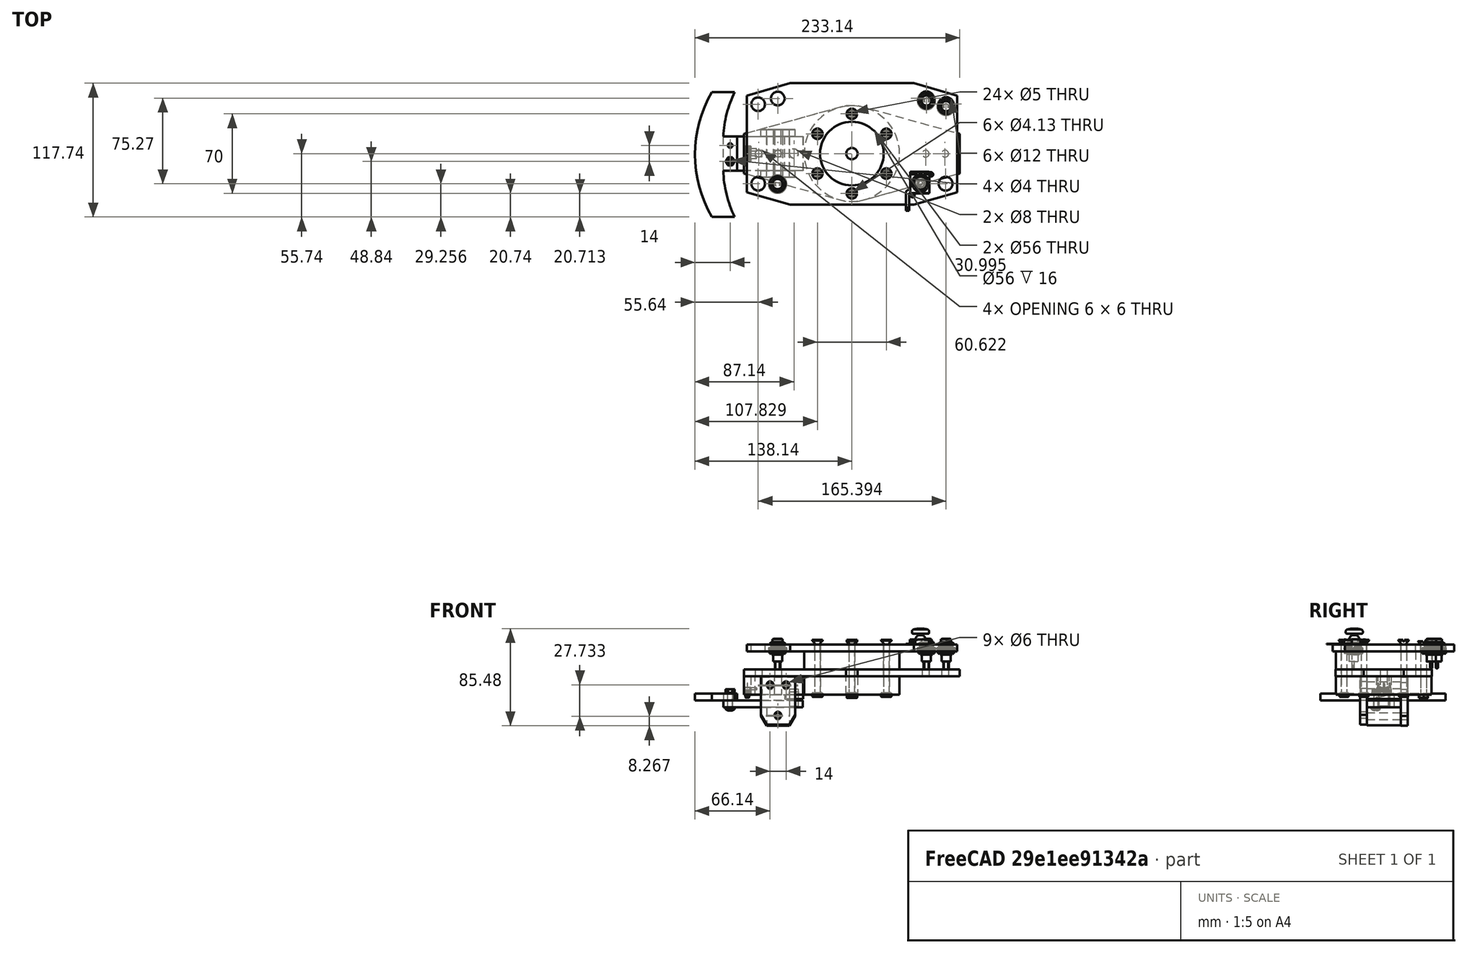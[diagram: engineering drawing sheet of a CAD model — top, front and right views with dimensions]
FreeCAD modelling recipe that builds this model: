
FCSTD DOCUMENT  (FreeCAD 0.19R24267 +99 (Git))
Label: Wheel
License: All rights reserved
LicenseURL: http://en.wikipedia.org/wiki/All_rights_reserved
objects: TechDraw::DrawViewDimension×38, Part::FeaturePython×16, TechDraw::DrawProjGroupItem×10, Sketcher::SketchObject×6, PartDesign::Pocket×6, App::Part×5, TechDraw::DrawProjGroup×5, PartDesign::Pad×4, PartDesign::ShapeBinder×4, PartDesign::Body×4, Part::Feature×3, TechDraw::DrawSVGTemplate×3, TechDraw::DrawPage×3, App::Link×2, PartDesign::SubShapeBinder×2, App::DocumentObjectGroup×1, Part::Mirroring×1
note: 56 computed .brp shape members not serialized (recipe doc carries the construction recipe); baked Part::Feature solids carry a one-line shape summary decoded from their .brp
EXTERNAL_REF file=PaddleShifter.FCStd obj=Part
EXTERNAL_REF file=PaddleShifter-v2.FCStd obj=Part

FEATURE [Part::Feature] steering_wheel_momo_team  label="steering_wheel_momo_team 300mm"
  Placement = pos=(3.67046e-10,8.97259,34) rot=(0,0,1;0rad)
  shape: bbox 319 x 576 x 33.23 mm, 603 faces, 0 solids (baked)
FEATURE [Sketcher::SketchObject] Sketch
  FullyConstrained = true
  MapMode = 5
  Support = -> [XY_Plane001]
  sketch-geometry (17):
    g0: Circle CenterX=-30.3109 CenterY=17.5 CenterZ=0 NormalX=0 NormalY=0 NormalZ=1 AngleXU=0 Radius=2.5
    g1: Circle CenterX=0 CenterY=35 CenterZ=0 NormalX=0 NormalY=0 NormalZ=1 AngleXU=0 Radius=2.5
    g2: Circle CenterX=30.3109 CenterY=17.5 CenterZ=0 NormalX=0 NormalY=0 NormalZ=1 AngleXU=0 Radius=2.5
    g3: Circle CenterX=30.3109 CenterY=-17.5 CenterZ=0 NormalX=0 NormalY=0 NormalZ=1 AngleXU=0 Radius=2.5
    g4: Circle CenterX=0 CenterY=-35 CenterZ=0 NormalX=0 NormalY=0 NormalZ=1 AngleXU=0 Radius=2.5
    g5: Circle CenterX=-30.3109 CenterY=-17.5 CenterZ=0 NormalX=0 NormalY=0 NormalZ=1 AngleXU=0 Radius=2.5
    g6: Circle CenterX=0 CenterY=0 CenterZ=0 NormalX=0 NormalY=0 NormalZ=1 AngleXU=0 Radius=35
    g7: LineSegment StartX=-30.3109 StartY=-17.5 StartZ=0 EndX=-30.3109 EndY=17.5 EndZ=0
    g8: LineSegment StartX=-30.3109 StartY=17.5 StartZ=0 EndX=0 EndY=35 EndZ=0
    g9: LineSegment StartX=0 StartY=35 StartZ=0 EndX=30.3109 EndY=17.5 EndZ=0
    g10: LineSegment StartX=30.3109 StartY=17.5 StartZ=0 EndX=30.3109 EndY=-17.5 EndZ=0
    g11: LineSegment StartX=30.3109 StartY=-17.5 StartZ=0 EndX=0 EndY=-35 EndZ=0
    g12: LineSegment StartX=-30.3109 StartY=-17.5 StartZ=0 EndX=0 EndY=-35 EndZ=0
    g13: Circle CenterX=0 CenterY=0 CenterZ=0 NormalX=0 NormalY=0 NormalZ=1 AngleXU=0 Radius=28
    g14: Circle CenterX=0 CenterY=0 CenterZ=0 NormalX=0 NormalY=0 NormalZ=1 AngleXU=0 Radius=42
    g15: LineSegment StartX=0 StartY=35 StartZ=0 EndX=0 EndY=42 EndZ=0
    g16: LineSegment StartX=0 StartY=35 StartZ=0 EndX=0 EndY=28 EndZ=0
  constraints (42):
    c: PointOnObject(g2,g6)
    c: PointOnObject(g1,g6)
    c: Coincident(g7,g5)
    c: Coincident(g7,g0)
    c: Coincident(g8,g0)
    c: Coincident(g8,g1)
    c: Coincident(g9,g1)
    c: Coincident(g9,g2)
    c: Coincident(g10,g2)
    c: Coincident(g10,g3)
    c: Coincident(g11,g3)
    c: Coincident(g11,g4)
    c: Coincident(g12,g5)
    c: Coincident(g12,g4)
    c: Coincident(g13,g6)
    c: Coincident(g14,g13)
    c: Coincident(g15,g1)
    c: PointOnObject(g15,g14)
    c: Vertical(g15)
    c: Coincident(g16,g1)
    c: PointOnObject(g16,g13)
    c: Vertical(g16)
    c: Equal(g15,g16)
    c: DistanceY(g15,g15) = 7
    c: Equal(g9,g8)
    c: Equal(g8,g7)
    c: Equal(g7,g12)
    c: Equal(g12,g11)
    c: Equal(g11,g10)
    c: Diameter(g1) = 5
    c: Equal(g1,g0)
    c: Equal(g0,g5)
    c: Equal(g5,g4)
    c: Equal(g4,g3)
    c: Equal(g3,g2)
    c: PointOnObject(g3,g6)
    c: PointOnObject(g4,g6)
    c: PointOnObject(g5,g6)
    c: PointOnObject(g1,g-2)
    c: PointOnObject(g4,g-2)
    c: Coincident(g-1,g13)
    c: Diameter(g6) = 70
FEATURE [PartDesign::Pad] Pad
  Direction = (1,1,1)
  Length = 16
  Length2 = 100
  Profile = -> Sketch
  Type = 0
FEATURE [PartDesign::ShapeBinder] ShapeBinder001
  Support = -> [Pad]
  TraceSupport = false
FEATURE [PartDesign::Pad] Pad001
  Direction = (1,1,1)
  Length = 16
  Length2 = 100
  Profile = -> ShapeBinder001
  Type = 0
FEATURE [Sketcher::SketchObject] Sketch001
  FullyConstrained = true
  MapMode = 5
  Placement = pos=(0,0,16) rot=(0,0,1;0rad)
  Support = -> [Pad001]
  sketch-geometry (1):
    g0: Circle CenterX=0 CenterY=0 CenterZ=0 NormalX=0 NormalY=0 NormalZ=1 AngleXU=0 Radius=5
  constraints (2):
    c: Coincident(g0,g-1)
    c: Diameter(g0) = 10
FEATURE [PartDesign::Pocket] Pocket
  BaseFeature = -> Pad001
  Length = 5
  Length2 = 100
  Profile = -> Sketch001
  Type = 1
FEATURE [PartDesign::Body] Body001  label="Ступица крепления"
  Group = -> [ShapeBinder001,Pad001,Sketch001,Pocket]
  Origin = -> Origin003
  Placement = pos=(0,0,-30) rot=(0,0,1;0rad)
  Tip = -> Pocket
FEATURE [PartDesign::ShapeBinder] ShapeBinder
  Placement = pos=(3.67046e-10,8.97259,34) rot=(0,0,1;0rad)
  Support = -> [steering_wheel_momo_team]
  TraceSupport = false
FEATURE [Sketcher::SketchObject] Sketch002  label="Размеры"
  ExternalGeometry = -> [ShapeBinder]
  FullyConstrained = true
  MapMode = 5
  Support = -> [XY_Plane001]
  sketch-geometry (4):
    g0: Circle CenterX=3.67046e-10 CenterY=34.9726 CenterZ=0 NormalX=0 NormalY=0 NormalZ=1 AngleXU=0 Radius=2.5
    g1: Circle CenterX=30.3109 CenterY=-17.5274 CenterZ=0 NormalX=0 NormalY=0 NormalZ=1 AngleXU=0 Radius=2.5
    g2: Circle CenterX=3.67046e-10 CenterY=-35.0274 CenterZ=0 NormalX=0 NormalY=0 NormalZ=1 AngleXU=0 Radius=2.5
    g3: Circle CenterX=0 CenterY=-0.0274115 CenterZ=0 NormalX=0 NormalY=0 NormalZ=1 AngleXU=0 Radius=35
  constraints (9):
    c: Coincident(g0,g-4)
    c: PointOnObject(g-4,g0)
    c: Coincident(g1,g-8)
    c: PointOnObject(g-8,g1)
    c: Coincident(g2,g-6)
    c: PointOnObject(g-6,g2)
    c: PointOnObject(g3,g-2)
    c: PointOnObject(g2,g3)
    c: PointOnObject(g1,g3)
FEATURE [PartDesign::Body] Body  label="Первая ступица"
  Group = -> [Sketch,Pad,ShapeBinder,Sketch002]
  Origin = -> Origin001
  Placement = pos=(0,0,-8) rot=(0,0,1;0rad)
  Tip = -> Pad
FEATURE [Sketcher::SketchObject] Sketch003
  FullyConstrained = false
  MapMode = 5
  Support = -> [XY_Plane004]
  sketch-geometry (18):
    g0: LineSegment StartX=-92.5 StartY=62 StartZ=0 EndX=92.5 EndY=62 EndZ=0
    g1: LineSegment StartX=92.5 StartY=62 StartZ=0 EndX=92.5 EndY=-45 EndZ=0
    g2: LineSegment StartX=92.5 StartY=-45 StartZ=0 EndX=-92.5 EndY=-45 EndZ=0
    g3: LineSegment StartX=-92.5 StartY=-45 StartZ=0 EndX=-92.5 EndY=62 EndZ=0
    g4: LineSegment StartX=92.5 StartY=-45 StartZ=0 EndX=92.5 EndY=100 EndZ=0
    g5: LineSegment StartX=-92.5 StartY=51 StartZ=0 EndX=-54.5 EndY=62 EndZ=0
    g6: LineSegment StartX=-92.5 StartY=-34 StartZ=0 EndX=-54.5 EndY=-45 EndZ=0
    g7: LineSegment StartX=92.5 StartY=51 StartZ=0 EndX=54.5 EndY=62 EndZ=0
    g8: LineSegment StartX=92.5 StartY=-34 StartZ=0 EndX=54.5 EndY=-45 EndZ=0
    g9: LineSegment StartX=-54.5 StartY=62 StartZ=0 EndX=54.5 EndY=62 EndZ=0
    g10: LineSegment StartX=-54.5 StartY=-45 StartZ=0 EndX=54.5 EndY=-45 EndZ=0
    g11: LineSegment StartX=-92.5 StartY=51 StartZ=0 EndX=-92.5 EndY=-34 EndZ=0
    g12: LineSegment StartX=92.5 StartY=51 StartZ=0 EndX=92.5 EndY=-34 EndZ=0
    g13: LineSegment StartX=-92.5 StartY=51 StartZ=0 EndX=-92.5 EndY=62 EndZ=0
    g14: LineSegment StartX=-92.5 StartY=62 StartZ=0 EndX=-54.5 EndY=62 EndZ=0
    g15: LineSegment StartX=-92.5 StartY=0 StartZ=0 EndX=0 EndY=0 EndZ=0
    g16: LineSegment StartX=0 StartY=0 StartZ=0 EndX=92.5 EndY=0 EndZ=0
    g17: LineSegment StartX=0 StartY=0 StartZ=0 EndX=0 EndY=-45 EndZ=0
  constraints (51):
    c: Coincident(g0,g1)
    c: Coincident(g1,g2)
    c: Coincident(g2,g3)
    c: Coincident(g3,g0)
    c: Horizontal(g0)
    c: Horizontal(g2)
    c: Vertical(g1)
    c: Vertical(g3)
    c: DistanceX(g0,g0) = 185
    c: DistanceY(g1,g1) = 107
    c: Vertical(g4)
    c: Coincident(g1,g4)
    c: PointOnObject(g5,g3)
    c: PointOnObject(g5,g0)
    c: PointOnObject(g6,g3)
    c: PointOnObject(g6,g2)
    c: Equal(g7,g5)
    c: Equal(g6,g5)
    c: Equal(g6,g8)
    c: PointOnObject(g8,g2)
    c: PointOnObject(g8,g1)
    c: PointOnObject(g7,g0)
    c: Parallel(g8,g5)
    c: Parallel(g7,g6)
    c: Coincident(g9,g5)
    c: Coincident(g9,g7)
    c: Coincident(g10,g6)
    c: Coincident(g10,g8)
    c: PointOnObject(g7,g1)
    c: Coincident(g11,g5)
    c: Coincident(g11,g6)
    c: Coincident(g12,g7)
    c: Coincident(g12,g8)
    c: Coincident(g13,g5)
    c: Coincident(g13,g0)
    c: Coincident(g14,g0)
    c: Coincident(g14,g5)
    c: Distance(g0,g5) = 11
    c: Distance(g5,g0) = 38
    c: Distance(g7,g0) = 38
    c: PointOnObject(g15,g11)
    c: Coincident(g15,g-1)
    c: Horizontal(g15)
    c: Coincident(g16,g-1)
    c: PointOnObject(g16,g12)
    c: Horizontal(g16)
    c: Coincident(g17,g-1)
    c: PointOnObject(g17,g10)
    c: Vertical(g17)
    c: Equal(g15,g16)
    c: DistanceY(g17,g17) = 45
FEATURE [PartDesign::Pad] Pad002
  Direction = (1,1,1)
  Length = 6
  Length2 = 100
  Profile = -> Sketch003
  Type = 0
FEATURE [PartDesign::ShapeBinder] ShapeBinder002
  Support = -> [Pad]
  TraceSupport = false
FEATURE [PartDesign::Pocket] Pocket001
  BaseFeature = -> Pad002
  Length = 5
  Length2 = 100
  Profile = -> ShapeBinder002
  Type = 1
FEATURE [Sketcher::SketchObject] Sketch004
  ExternalGeometry = -> [Pocket001]
  FullyConstrained = false
  MapMode = 5
  Placement = pos=(0,0,6) rot=(0,0,1;0rad)
  Support = -> [Pocket001]
  sketch-geometry (10):
    g0: LineSegment StartX=-92.5 StartY=40.5895 StartZ=0 EndX=-15.5219 EndY=62.8726 EndZ=0
    g1: Circle CenterX=-82.5 CenterY=43.4842 CenterZ=0 NormalX=0 NormalY=0 NormalZ=1 AngleXU=0 Radius=6
    g2: Circle CenterX=-65.2098 CenterY=48.4892 CenterZ=0 NormalX=0 NormalY=0 NormalZ=1 AngleXU=0 Radius=6
    g3: Circle CenterX=-82.5 CenterY=-26.4842 CenterZ=0 NormalX=0 NormalY=0 NormalZ=1 AngleXU=0 Radius=6
    g4: LineSegment StartX=-92.2324 StartY=-23.6669 StartZ=0 EndX=-34.7028 EndY=-40.3202 EndZ=0
    g5: Circle CenterX=65.6042 CenterY=48.7856 CenterZ=0 NormalX=0 NormalY=0 NormalZ=1 AngleXU=0 Radius=6
    g6: Circle CenterX=82.8944 CenterY=43.7806 CenterZ=0 NormalX=0 NormalY=0 NormalZ=1 AngleXU=0 Radius=6
    g7: LineSegment StartX=92.5 StartY=41 StartZ=0 EndX=13.4764 EndY=63.8753 EndZ=0
    g8: LineSegment StartX=92.5 StartY=-23.5895 StartZ=0 EndX=48.0012 EndY=-36.4707 EndZ=0
    g9: Circle CenterX=82.5 CenterY=-26.4842 CenterZ=0 NormalX=0 NormalY=0 NormalZ=1 AngleXU=0 Radius=6
  constraints (29):
    c: Parallel(g0,g-3)
    c: PointOnObject(g1,g0)
    c: PointOnObject(g2,g0)
    c: Diameter(g2) = 12
    c: Equal(g2,g1)
    c: Equal(g3,g1)
    c: Parallel(g4,g-9)
    c: PointOnObject(g3,g4)
    c: PointOnObject(g0,g-10)
    c: Distance(g2,g-3) = 10
    c: Distance(g1,g2) = 18
    c: Distance(g3,g-10) = 10
    c: Distance(g1,g-10) = 10
    c: Diameter(g5) = 12
    c: Equal(g5,g6)
    c: PointOnObject(g7,g-6)
    c: Parallel(g7,g-5)
    c: PointOnObject(g6,g7)
    c: PointOnObject(g5,g7)
    c: Distance(g7,g-6) = 10
    c: Distance(g6,g7) = 10
    c: Distance(g5,g6) = 18
    c: Distance(g-9,g4) = 10
    c: PointOnObject(g8,g-6)
    c: Parallel(g8,g-7)
    c: PointOnObject(g9,g8)
    c: Equal(g9,g3)
    c: Distance(g9,g-6) = 10
    c: Distance(g-8,g8) = 10
FEATURE [PartDesign::Pocket] Pocket002
  BaseFeature = -> Pocket001
  Length = 5
  Length2 = 100
  Profile = -> Sketch004
  Type = 1
FEATURE [PartDesign::Body] Body002  label="Панель для кнопок"
  Group = -> [Sketch003,Pad002,Sketch004,ShapeBinder002,Pocket001,Pocket002]
  Origin = -> Origin004
  Placement = pos=(0,0,8) rot=(0,0,1;0rad)
  Tip = -> Pocket002
FEATURE [Part::Feature] Feature  label="Switch Joystick001"
  Placement = pos=(52,-21,29) rot=(1,0,0;1.5708rad)
  shape: bbox 24.16 x 34.22 x 14 mm, 272 faces, 2 solids (baked)
FEATURE [Part::Feature] Compound  label="push_button_SGI_R13-502"
  Placement = pos=(-82.5,41.4842,19.1) rot=(0,1,0;1.5708rad)
  shape: bbox 16.11 x 16.16 x 26.1 mm, 217 faces (baked)
FEATURE [Part::FeaturePython] Clone  label="push_button_SGI_R13-503"  # Draft clone (typed FeaturePython)
  AttacherType = Attacher::AttachEngine3D
  Fuse = false
  Objects = -> [Compound]
  Placement = pos=(-65.2098,46.4892,19.1) rot=(0,1,0;1.5708rad)
  Scale = (1,1,1)
  Support = -> [Pocket002,Sketch004]
FEATURE [Part::FeaturePython] Clone001  label="push_button_SGI_R13-504"  # Draft clone (typed FeaturePython)
  AttacherType = Attacher::AttachEngine3D
  Fuse = false
  Objects = -> [Clone]
  Placement = pos=(-65.3944,-26.7806,19.1) rot=(0,1,0;1.5708rad)
  Scale = (1,1,1)
FEATURE [Part::FeaturePython] Clone002  label="push_button_SGI_R13-505"  # Draft clone (typed FeaturePython)
  AttacherType = Attacher::AttachEngine3D
  Fuse = false
  Objects = -> [Clone]
  Placement = pos=(82.8944,41.7806,19.1) rot=(0,1,0;1.5708rad)
  Scale = (1,1,1)
FEATURE [Part::FeaturePython] Clone003  label="push_button_SGI_R13-506"  # Draft clone (typed FeaturePython)
  AttacherType = Attacher::AttachEngine3D
  Fuse = false
  Objects = -> [Clone]
  Placement = pos=(65.6042,46.7856,19.1) rot=(0,1,0;1.5708rad)
  Scale = (1,1,1)
FEATURE [App::Part] Part002  label="Кнопки"
  Group = -> [Compound,Clone,Clone003,Clone002,Clone001]
  Origin = -> Origin005
FEATURE [Sketcher::SketchObject] Sketch005
  FullyConstrained = true
  MapMode = 5
  Support = -> [XY_Plane006]
  sketch-geometry (13):
    g0: LineSegment StartX=-95 StartY=42.5 StartZ=0 EndX=95 EndY=42.5 EndZ=0
    g1: LineSegment StartX=95 StartY=42.5 StartZ=0 EndX=95 EndY=-42.5 EndZ=0
    g2: LineSegment StartX=95 StartY=-42.5 StartZ=0 EndX=-95 EndY=-42.5 EndZ=0
    g3: LineSegment StartX=-95 StartY=-42.5 StartZ=0 EndX=-95 EndY=42.5 EndZ=0
    g4: LineSegment StartX=-5 StartY=42.5 StartZ=0 EndX=5 EndY=42.5 EndZ=0
    g5: LineSegment StartX=5 StartY=42.5 StartZ=0 EndX=95 EndY=17.5 EndZ=0
    g6: LineSegment StartX=95 StartY=17.5 StartZ=0 EndX=95 EndY=-17.5 EndZ=0
    g7: LineSegment StartX=95 StartY=-17.5 StartZ=0 EndX=5 EndY=-42.5 EndZ=0
    g8: LineSegment StartX=5 StartY=-42.5 StartZ=0 EndX=-5 EndY=-42.5 EndZ=0
    g9: LineSegment StartX=-5 StartY=-42.5 StartZ=0 EndX=-95 EndY=-17.5 EndZ=0
    g10: LineSegment StartX=-95 StartY=-17.5 StartZ=0 EndX=-95 EndY=17.5 EndZ=0
    g11: LineSegment StartX=-95 StartY=17.5 StartZ=0 EndX=-5 EndY=42.5 EndZ=0
    g12: GeomPoint X=-95 Y=0 Z=0
  constraints (36):
    c: Coincident(g0,g1)
    c: Coincident(g1,g2)
    c: Coincident(g2,g3)
    c: Coincident(g3,g0)
    c: Horizontal(g0)
    c: Horizontal(g2)
    c: Vertical(g1)
    c: Vertical(g3)
    c: Symmetric(g0,g2,g-1)
    c: PointOnObject(g4,g0)
    c: PointOnObject(g4,g0)
    c: Coincident(g5,g4)
    c: PointOnObject(g5,g1)
    c: Coincident(g6,g5)
    c: PointOnObject(g6,g1)
    c: Coincident(g7,g6)
    c: PointOnObject(g7,g2)
    c: Coincident(g8,g7)
    c: PointOnObject(g8,g2)
    c: Coincident(g9,g8)
    c: PointOnObject(g9,g3)
    c: Coincident(g10,g9)
    c: PointOnObject(g10,g3)
    c: Coincident(g11,g10)
    c: Coincident(g11,g4)
    c: Equal(g4,g8)
    c: Equal(g10,g6)
    c: Parallel(g11,g7)
    c: Equal(g11,g7)
    c: Equal(g11,g5)
    c: DistanceY(g1,g1) = 85
    c: DistanceX(g0,g0) = 190
    c: DistanceY(g10,g10) = 35
    c: PointOnObject(g12,g-1)
    c: Symmetric(g10,g9,g12)
    c: DistanceX(g4,g4) = 10
FEATURE [PartDesign::Pad] Pad003
  Direction = (1,1,1)
  Length = 6
  Length2 = 100
  Profile = -> Sketch005
  Type = 0
FEATURE [PartDesign::ShapeBinder] ShapeBinder003
  Support = -> [Pad]
  TraceSupport = false
FEATURE [PartDesign::Pocket] Pocket003
  BaseFeature = -> Pad003
  Length = 5
  Length2 = 100
  Profile = -> ShapeBinder003
  Reversed = true
  Type = 1
FEATURE [Part::FeaturePython] Screw  label="M5x50-Screw"  # Fasteners workbench fastener (typed FeaturePython)
  Placement = pos=(3.67046e-10,34.9726,17) rot=(0,0,1;0rad)
  baseObject = -> steering_wheel_momo_team [Edge1689]
  diameter = 7
  invert = true
  length = 11
  lengthCustom = 50
  matchOuter = false
  offset = 2
  thread = false
  type = 26
FEATURE [Part::FeaturePython] Screw001  label="M5x50-Screw001"  # Fasteners workbench fastener (typed FeaturePython)
  Placement = pos=(-30.3109,17.4726,18) rot=(0,0,1;0rad)
  baseObject = -> steering_wheel_momo_team [Edge1628]
  diameter = 7
  invert = false
  length = 11
  lengthCustom = 50
  matchOuter = false
  offset = 3
  thread = false
  type = 26
FEATURE [Part::FeaturePython] Screw002  label="M5x50-Screw002"  # Fasteners workbench fastener (typed FeaturePython)
  Placement = pos=(30.3109,17.4726,18) rot=(0,0,1;0rad)
  baseObject = -> steering_wheel_momo_team [Edge1693]
  diameter = 7
  invert = true
  length = 11
  lengthCustom = 50
  matchOuter = false
  offset = 3
  thread = false
  type = 26
FEATURE [Part::FeaturePython] Screw003  label="M5x50-Screw003"  # Fasteners workbench fastener (typed FeaturePython)
  Placement = pos=(-30.3109,-17.5274,18) rot=(0,0,1;0rad)
  baseObject = -> steering_wheel_momo_team [Edge1705]
  diameter = 7
  invert = true
  length = 11
  lengthCustom = 50
  matchOuter = false
  offset = 3
  thread = false
  type = 26
FEATURE [Part::FeaturePython] Screw004  label="M5x50-Screw004"  # Fasteners workbench fastener (typed FeaturePython)
  Placement = pos=(3.67046e-10,-35.0274,18) rot=(0,0,1;0rad)
  baseObject = -> steering_wheel_momo_team [Edge1701]
  diameter = 7
  invert = true
  length = 11
  lengthCustom = 50
  matchOuter = false
  offset = 3
  thread = false
  type = 26
FEATURE [Part::FeaturePython] Screw005  label="M5x50-Screw005"  # Fasteners workbench fastener (typed FeaturePython)
  Placement = pos=(30.3109,-17.5274,18) rot=(0,0,1;0rad)
  baseObject = -> steering_wheel_momo_team [Edge1697]
  diameter = 7
  invert = true
  length = 11
  lengthCustom = 50
  matchOuter = false
  offset = 3
  thread = false
  type = 26
FEATURE [Part::FeaturePython] Nut  label="M5-Nut"  # Fasteners workbench fastener (typed FeaturePython)
  Placement = pos=(3.67046e-10,34.9726,-33) rot=(0,0,1;0rad)
  baseObject = -> Screw [Edge26]
  diameter = 7
  invert = false
  matchOuter = false
  offset = 0
  thread = false
  type = 7
FEATURE [Part::FeaturePython] Nut001  label="M5-Nut001"  # Fasteners workbench fastener (typed FeaturePython)
  Placement = pos=(-30.3109,17.4726,-32) rot=(0,0,1;0rad)
  baseObject = -> Screw001 [Edge26]
  diameter = 7
  invert = false
  matchOuter = false
  offset = 0
  thread = false
  type = 7
FEATURE [Part::FeaturePython] Nut002  label="M5-Nut002"  # Fasteners workbench fastener (typed FeaturePython)
  Placement = pos=(-30.3109,-17.5274,-32) rot=(0,0,1;0rad)
  baseObject = -> Screw003 [Edge26]
  diameter = 7
  invert = false
  matchOuter = false
  offset = 0
  thread = false
  type = 7
FEATURE [Part::FeaturePython] Nut003  label="M5-Nut003"  # Fasteners workbench fastener (typed FeaturePython)
  Placement = pos=(3.67046e-10,-35.0274,-32) rot=(0,0,1;0rad)
  baseObject = -> Screw004 [Edge26]
  diameter = 7
  invert = false
  matchOuter = false
  offset = 0
  thread = false
  type = 7
FEATURE [Part::FeaturePython] Nut004  label="M5-Nut004"  # Fasteners workbench fastener (typed FeaturePython)
  Placement = pos=(30.3109,-17.5274,-32) rot=(0,0,1;0rad)
  baseObject = -> Screw005 [Edge26]
  diameter = 7
  invert = false
  matchOuter = false
  offset = 0
  thread = false
  type = 7
FEATURE [Part::FeaturePython] Nut005  label="M5-Nut005"  # Fasteners workbench fastener (typed FeaturePython)
  Placement = pos=(30.3109,17.4726,-32) rot=(0,0,1;0rad)
  baseObject = -> Screw002 [Edge26]
  diameter = 7
  invert = false
  matchOuter = false
  offset = 0
  thread = false
  type = 7
FEATURE [App::Part] Part003  label="Болты"
  Group = -> [Screw,Screw001,Screw002,Screw003,Screw004,Screw005,Nut,Nut001,Nut002,Nut003,Nut004,Nut005]
  Origin = -> Origin007
FEATURE [TechDraw::DrawSVGTemplate] Template
  Height = 210
  Orientation = 1
  Width = 297
FEATURE [TechDraw::DrawProjGroupItem] ProjItem  label="Front"
  CoarseView = false
  Direction = (0,0,1)
  Focus = 100
  HardHidden = false
  IsoCount = 0
  IsoHidden = false
  IsoVisible = false
  LockPosition = true
  Perspective = false
  Rotation = 0
  RotationVector = (1,0,0)
  ScaleType = 2
  SeamHidden = false
  SeamVisible = true
  SmoothHidden = false
  SmoothVisible = true
  Source = -> [Body]
  Type = 0
  X = 0
  XDirection = (1,0,0)
  Y = 0
FEATURE [TechDraw::DrawProjGroupItem] ProjItem001  label="Left"
  CoarseView = false
  Direction = (-1,0,1e-16)
  Focus = 100
  HardHidden = false
  IsoCount = 0
  IsoHidden = false
  IsoVisible = false
  LockPosition = true
  Perspective = false
  Rotation = 0
  RotationVector = (1,0,0)
  ScaleType = 2
  SeamHidden = false
  SeamVisible = true
  SmoothHidden = false
  SmoothVisible = true
  Source = -> [Body]
  Type = 1
  X = 71.4433
  XDirection = (1e-16,0,1)
  Y = 0
FEATURE [TechDraw::DrawProjGroupItem] ProjItem002  label="FrontBottomLeft"
  CoarseView = false
  Direction = (-0.57735,-0.57735,0.57735)
  Focus = 100
  HardHidden = false
  IsoCount = 0
  IsoHidden = false
  IsoVisible = false
  LockPosition = true
  Perspective = false
  Rotation = 0
  RotationVector = (1,0,0)
  ScaleType = 2
  SeamHidden = false
  SeamVisible = true
  SmoothHidden = false
  SmoothVisible = true
  Source = -> [Body]
  Type = 8
  X = 131.211
  XDirection = (0.707107,0,0.707107)
  Y = -2.68994
FEATURE [TechDraw::DrawProjGroup] ProjGroup
  Anchor = -> ProjItem
  AutoDistribute = true
  LockPosition = true
  ProjectionType = 0
  Rotation = 0
  ScaleType = 0
  Source = -> [Body]
  Views = -> [ProjItem,ProjItem001,ProjItem002]
  X = 77.7723
  Y = 148.663
  spacingX = 15
  spacingY = 15
FEATURE [TechDraw::DrawViewDimension] Dimension
  Arbitrary = false
  ArbitraryTolerances = false
  EqualTolerance = true
  FormatSpec = ⌀%.2f
  FormatSpecOverTolerance = %+.2f
  FormatSpecUnderTolerance = %+.2f
  Inverted = false
  LockPosition = false
  MeasureType = 1
  OverTolerance = 0
  References2D = -> [ProjItem]
  Rotation = 0
  ScaleType = 0
  TheoreticalExact = false
  Type = 5
  UnderTolerance = 0
  X = 44.6718
  Y = 35.8477
FEATURE [TechDraw::DrawViewDimension] Dimension001
  Arbitrary = false
  ArbitraryTolerances = false
  EqualTolerance = true
  FormatSpec = ⌀%.2f
  FormatSpecOverTolerance = %+.2f
  FormatSpecUnderTolerance = %+.2f
  Inverted = false
  LockPosition = false
  MeasureType = 1
  OverTolerance = 0
  References2D = -> [ProjItem]
  Rotation = 0
  ScaleType = 0
  TheoreticalExact = false
  Type = 5
  UnderTolerance = 0
  X = 47.9808
  Y = 24.4237
FEATURE [TechDraw::DrawViewDimension] Dimension002
  Arbitrary = false
  ArbitraryTolerances = false
  EqualTolerance = true
  FormatSpec = ⌀%.2f
  FormatSpecOverTolerance = %+.2f
  FormatSpecUnderTolerance = %+.2f
  Inverted = false
  LockPosition = false
  MeasureType = 1
  OverTolerance = 0
  References2D = -> [ProjItem]
  Rotation = 0
  ScaleType = 0
  TheoreticalExact = false
  Type = 5
  UnderTolerance = 0
  X = 48.7293
  Y = -1.26058
FEATURE [TechDraw::DrawViewDimension] Dimension003
  Arbitrary = false
  ArbitraryTolerances = false
  EqualTolerance = true
  FormatSpec = %.2f
  FormatSpecOverTolerance = %+.2f
  FormatSpecUnderTolerance = %+.2f
  Inverted = false
  LockPosition = false
  MeasureType = 1
  OverTolerance = 0
  References2D = -> [ProjItem]
  Rotation = 0
  ScaleType = 0
  TheoreticalExact = false
  Type = 0
  UnderTolerance = 0
  X = -25.5836
  Y = 41.3536
FEATURE [TechDraw::DrawViewDimension] Dimension004
  Arbitrary = false
  ArbitraryTolerances = false
  EqualTolerance = true
  FormatSpec = %.2f
  FormatSpecOverTolerance = %+.2f
  FormatSpecUnderTolerance = %+.2f
  Inverted = false
  LockPosition = false
  MeasureType = 1
  OverTolerance = 0
  References2D = -> [ProjItem]
  Rotation = 0
  ScaleType = 0
  TheoreticalExact = false
  Type = 2
  UnderTolerance = 0
  X = -8.66649
  Y = 19.2727
FEATURE [TechDraw::DrawViewDimension] Dimension005
  Arbitrary = false
  ArbitraryTolerances = false
  EqualTolerance = true
  FormatSpec = %.2f
  FormatSpecOverTolerance = %+.2f
  FormatSpecUnderTolerance = %+.2f
  Inverted = false
  LockPosition = false
  MeasureType = 1
  OverTolerance = 0
  References2D = -> [ProjItem]
  Rotation = 0
  ScaleType = 0
  TheoreticalExact = false
  Type = 0
  UnderTolerance = 0
  X = 8.06468
  Y = -12.6893
FEATURE [TechDraw::DrawViewDimension] Dimension006
  Arbitrary = false
  ArbitraryTolerances = false
  EqualTolerance = true
  FormatSpec = %.2f
  FormatSpecOverTolerance = %+.2f
  FormatSpecUnderTolerance = %+.2f
  Inverted = false
  LockPosition = false
  MeasureType = 1
  OverTolerance = 0
  References2D = -> [ProjItem001]
  Rotation = 0
  ScaleType = 0
  TheoreticalExact = false
  Type = 1
  UnderTolerance = 0
  X = -0.11862
  Y = -6.8078
FEATURE [TechDraw::DrawProjGroupItem] ProjItem003  label="Front001"
  CoarseView = false
  Direction = (0,0,1)
  Focus = 100
  HardHidden = false
  IsoCount = 0
  IsoHidden = false
  IsoVisible = false
  LockPosition = true
  Perspective = false
  Rotation = 0
  RotationVector = (1,0,0)
  ScaleType = 2
  SeamHidden = false
  SeamVisible = true
  SmoothHidden = false
  SmoothVisible = true
  Source = -> [Body001]
  Type = 0
  X = 0
  XDirection = (1,0,0)
  Y = 0
FEATURE [TechDraw::DrawProjGroupItem] ProjItem004  label="FrontBottomLeft001"
  CoarseView = false
  Direction = (-0.57735,-0.57735,0.57735)
  Focus = 100
  HardHidden = false
  IsoCount = 0
  IsoHidden = false
  IsoVisible = false
  LockPosition = true
  Perspective = false
  Rotation = 0
  RotationVector = (1,0,0)
  ScaleType = 2
  SeamHidden = false
  SeamVisible = true
  SmoothHidden = false
  SmoothVisible = true
  Source = -> [Body001]
  Type = 8
  X = 83.5882
  XDirection = (0.707107,0,0.707107)
  Y = -2.01571
FEATURE [TechDraw::DrawProjGroup] ProjGroup001
  Anchor = -> ProjItem003
  AutoDistribute = true
  LockPosition = true
  ProjectionType = 0
  Rotation = 0
  ScaleType = 0
  Source = -> [Body001]
  Views = -> [ProjItem003,ProjItem004]
  X = 78.0159
  Y = 58.4258
  spacingX = 15
  spacingY = 15
FEATURE [TechDraw::DrawViewDimension] Dimension007
  Arbitrary = false
  ArbitraryTolerances = false
  EqualTolerance = true
  FormatSpec = ⌀%.2f
  FormatSpecOverTolerance = %+.2f
  FormatSpecUnderTolerance = %+.2f
  Inverted = false
  LockPosition = false
  MeasureType = 1
  OverTolerance = 0
  References2D = -> [ProjItem003]
  Rotation = 0
  ScaleType = 0
  TheoreticalExact = false
  Type = 5
  UnderTolerance = 0
  X = 9.18963
  Y = 18.7196
FEATURE [TechDraw::DrawPage] Page  label="Ступица"
  KeepUpdated = true
  NextBalloonIndex = 1
  ProjectionType = 0
  Template = -> Template
  Views = -> [ProjGroup,Dimension,Dimension001,Dimension002,Dimension003,Dimension004,Dimension005,Dimension006,ProjGroup001,Dimension007]
FEATURE [TechDraw::DrawSVGTemplate] Template001
  Height = 210
  Orientation = 1
  Width = 297
FEATURE [TechDraw::DrawProjGroupItem] ProjItem005  label="Front002"
  CoarseView = false
  Direction = (0,0,1)
  Focus = 100
  HardHidden = false
  IsoCount = 0
  IsoHidden = false
  IsoVisible = false
  LockPosition = true
  Perspective = false
  Rotation = 0
  RotationVector = (1,0,0)
  ScaleType = 2
  SeamHidden = false
  SeamVisible = true
  SmoothHidden = false
  SmoothVisible = true
  Source = -> [Body002]
  Type = 0
  X = 0
  XDirection = (1,0,0)
  Y = 0
FEATURE [TechDraw::DrawViewDimension] Dimension008
  Arbitrary = false
  ArbitraryTolerances = false
  EqualTolerance = true
  FormatSpec = 5 ⌀%.2f
  FormatSpecOverTolerance = %+.2f
  FormatSpecUnderTolerance = %+.2f
  Inverted = false
  LockPosition = false
  MeasureType = 1
  OverTolerance = 0
  References2D = -> [ProjItem005]
  Rotation = 0
  ScaleType = 0
  TheoreticalExact = false
  Type = 5
  UnderTolerance = 0
  X = -81.1498
  Y = 23.9394
FEATURE [TechDraw::DrawViewDimension] Dimension011
  Arbitrary = false
  ArbitraryTolerances = false
  EqualTolerance = true
  FormatSpec = %.2f
  FormatSpecOverTolerance = %+.2f
  FormatSpecUnderTolerance = %+.2f
  Inverted = false
  LockPosition = false
  MeasureType = 1
  OverTolerance = 0
  References2D = -> [ProjItem005]
  Rotation = 0
  ScaleType = 0
  TheoreticalExact = false
  Type = 1
  UnderTolerance = 0
  X = -63.4419
  Y = -37.0776
FEATURE [TechDraw::DrawViewDimension] Dimension012
  Arbitrary = false
  ArbitraryTolerances = false
  EqualTolerance = true
  FormatSpec = %.2f
  FormatSpecOverTolerance = %+.2f
  FormatSpecUnderTolerance = %+.2f
  Inverted = false
  LockPosition = false
  MeasureType = 1
  OverTolerance = 0
  References2D = -> [ProjItem005]
  Rotation = 0
  ScaleType = 0
  TheoreticalExact = false
  Type = 1
  UnderTolerance = 0
  X = 1.00126
  Y = -55.9985
FEATURE [TechDraw::DrawViewDimension] Dimension013
  Arbitrary = false
  ArbitraryTolerances = false
  EqualTolerance = true
  FormatSpec = %.2f
  FormatSpecOverTolerance = %+.2f
  FormatSpecUnderTolerance = %+.2f
  Inverted = false
  LockPosition = false
  MeasureType = 1
  OverTolerance = 0
  References2D = -> [ProjItem005]
  Rotation = 0
  ScaleType = 0
  TheoreticalExact = false
  Type = 2
  UnderTolerance = 0
  X = -103.321
  Y = 11.5289
FEATURE [TechDraw::DrawViewDimension] Dimension014
  Arbitrary = false
  ArbitraryTolerances = false
  EqualTolerance = true
  FormatSpec = %.2f
  FormatSpecOverTolerance = %+.2f
  FormatSpecUnderTolerance = %+.2f
  Inverted = false
  LockPosition = false
  MeasureType = 1
  OverTolerance = 0
  References2D = -> [ProjItem005]
  Rotation = 0
  ScaleType = 0
  TheoreticalExact = false
  Type = 1
  UnderTolerance = 0
  X = -81.4282
  Y = -50.3121
FEATURE [TechDraw::DrawViewDimension] Dimension016
  Arbitrary = false
  ArbitraryTolerances = false
  EqualTolerance = true
  FormatSpec = ⌀%.2f
  FormatSpecOverTolerance = %+.2f
  FormatSpecUnderTolerance = %+.2f
  Inverted = false
  LockPosition = false
  MeasureType = 1
  OverTolerance = 0
  References2D = -> [ProjItem005]
  Rotation = 0
  ScaleType = 0
  TheoreticalExact = false
  Type = 5
  UnderTolerance = 0
  X = 46.5495
  Y = 18.1026
FEATURE [TechDraw::DrawViewDimension] Dimension022
  Arbitrary = false
  ArbitraryTolerances = false
  EqualTolerance = true
  FormatSpec = %.2f
  FormatSpecOverTolerance = %+.2f
  FormatSpecUnderTolerance = %+.2f
  Inverted = false
  LockPosition = false
  MeasureType = 1
  OverTolerance = 0
  References2D = -> [ProjItem005]
  Rotation = 0
  ScaleType = 0
  TheoreticalExact = false
  Type = 1
  UnderTolerance = 0
  X = 2.9493
  Y = -64.7567
FEATURE [TechDraw::DrawProjGroupItem] ProjItem007  label="Top"
  CoarseView = false
  Direction = (0,1,0)
  Focus = 100
  HardHidden = false
  IsoCount = 0
  IsoHidden = false
  IsoVisible = false
  LockPosition = true
  Perspective = false
  Rotation = 0
  RotationVector = (1,0,0)
  ScaleType = 2
  SeamHidden = false
  SeamVisible = true
  SmoothHidden = false
  SmoothVisible = true
  Source = -> [Body002]
  Type = 4
  X = 0
  XDirection = (1,0,0)
  Y = -92.1638
FEATURE [TechDraw::DrawProjGroup] ProjGroup002
  Anchor = -> ProjItem005
  AutoDistribute = true
  LockPosition = true
  ProjectionType = 0
  Rotation = 0
  ScaleType = 0
  Source = -> [Body002]
  Views = -> [ProjItem005,ProjItem007]
  X = 149.949
  Y = 126.903
  spacingX = 15
  spacingY = 15
FEATURE [TechDraw::DrawViewDimension] Dimension023
  Arbitrary = false
  ArbitraryTolerances = false
  EqualTolerance = true
  FormatSpec = %.2f
  FormatSpecOverTolerance = %+.2f
  FormatSpecUnderTolerance = %+.2f
  Inverted = false
  LockPosition = false
  MeasureType = 1
  OverTolerance = 0
  References2D = -> [ProjItem007]
  Rotation = 0
  ScaleType = 0
  TheoreticalExact = false
  Type = 2
  UnderTolerance = 0
  X = -82.3975
  Y = 0.965629
FEATURE [TechDraw::DrawSVGTemplate] Template002
  Height = 210
  Orientation = 1
  Width = 297
FEATURE [TechDraw::DrawProjGroupItem] ProjItem010  label="Front004"
  CoarseView = false
  Direction = (0.483,0.564,0.67)
  Focus = 100
  HardHidden = false
  IsoCount = 0
  IsoHidden = false
  IsoVisible = false
  LockPosition = true
  Perspective = false
  Rotation = 0
  RotationVector = (0.751,0.127,-0.648)
  ScaleType = 2
  SeamHidden = false
  SeamVisible = true
  SmoothHidden = false
  SmoothVisible = true
  Type = 0
  X = 0
  XDirection = (0.751,0.127,-0.648)
  Y = 0
FEATURE [TechDraw::DrawProjGroup] ProjGroup004
  Anchor = -> ProjItem010
  AutoDistribute = true
  LockPosition = false
  ProjectionType = 0
  Rotation = 0
  ScaleType = 0
  Views = -> [ProjItem010]
  X = 264.657
  Y = 42.3083
  spacingX = 15
  spacingY = 15
FEATURE [App::Link] Link  label="PaddleShifter"
  LinkPlacement = pos=(65,1.51e-05,-14) rot=(1,0,0;3.14159rad)
  LinkedObject = -> <external PaddleShifter.FCStd>#Part
  Placement = pos=(65,1.51e-05,-14) rot=(1,0,0;3.14159rad)
FEATURE [PartDesign::SubShapeBinder] Binder
  BindMode = 0
  ClaimChildren = false
  Context = -> Part [Part001.Part004.Body003.Binder.]
  Fuse = false
  MakeFace = true
  PartialLoad = false
  Relative = true
  Support = -> [Link[Body.Pocket005.Edge17,Body.Pocket005.Edge16]]
  _Version = 2
FEATURE [PartDesign::Pocket] Pocket004
  BaseFeature = -> Pocket003
  Length = 5
  Length2 = 100
  Midplane = true
  Profile = -> Binder
  Reversed = true
  Type = 1
FEATURE [PartDesign::SubShapeBinder] Binder001
  BindMode = 0
  ClaimChildren = false
  Context = -> Part [Part001.Part004.Body003.Binder001.]
  Fuse = false
  MakeFace = true
  PartialLoad = false
  Relative = true
  _Version = 2
FEATURE [PartDesign::Pocket] Pocket005
  BaseFeature = -> Pocket004
  Length = 5
  Length2 = 100
  Midplane = true
  Profile = -> Binder001
  Reversed = true
  Type = 1
FEATURE [PartDesign::Body] Body003  label="Крепление лепестков"
  Group = -> [Sketch005,Pad003,ShapeBinder003,Pocket003,Binder,Pocket004,Binder001,Pocket005]
  Origin = -> Origin006
  Placement = pos=(0,0,-14) rot=(0,0,1;0rad)
  Tip = -> Pocket005
FEATURE [TechDraw::DrawProjGroupItem] ProjItem008  label="Front003"
  CoarseView = false
  Direction = (0,0,1)
  Focus = 100
  HardHidden = false
  IsoCount = 0
  IsoHidden = false
  IsoVisible = false
  LockPosition = true
  Perspective = false
  Rotation = 0
  RotationVector = (1,0,0)
  ScaleType = 2
  SeamHidden = false
  SeamVisible = true
  SmoothHidden = false
  SmoothVisible = true
  Source = -> [Body003]
  Type = 0
  X = 0
  XDirection = (1,0,0)
  Y = 0
FEATURE [TechDraw::DrawProjGroupItem] ProjItem009  label="Top001"
  CoarseView = false
  Direction = (0,1,0)
  Focus = 100
  HardHidden = false
  IsoCount = 0
  IsoHidden = false
  IsoVisible = false
  LockPosition = true
  Perspective = false
  Rotation = 0
  RotationVector = (1,0,0)
  ScaleType = 2
  SeamHidden = false
  SeamVisible = true
  SmoothHidden = false
  SmoothVisible = true
  Source = -> [Body003]
  Type = 4
  X = 0
  XDirection = (1,0,0)
  Y = -68.0408
FEATURE [TechDraw::DrawProjGroup] ProjGroup003
  Anchor = -> ProjItem008
  AutoDistribute = true
  LockPosition = false
  ProjectionType = 0
  Rotation = 0
  ScaleType = 0
  Source = -> [Body003]
  Views = -> [ProjItem008,ProjItem009]
  X = 146.963
  Y = 115.277
  spacingX = 15
  spacingY = 15
FEATURE [TechDraw::DrawViewDimension] Dimension024
  Arbitrary = false
  ArbitraryTolerances = false
  EqualTolerance = true
  FormatSpec = %.2f
  FormatSpecOverTolerance = %+.2f
  FormatSpecUnderTolerance = %+.2f
  Inverted = false
  LockPosition = false
  MeasureType = 1
  OverTolerance = 0
  References2D = -> [ProjItem008]
  Rotation = 0
  ScaleType = 0
  TheoreticalExact = false
  Type = 2
  UnderTolerance = 0
  X = -107.398
  Y = -0.528034
FEATURE [TechDraw::DrawViewDimension] Dimension025
  Arbitrary = false
  ArbitraryTolerances = false
  EqualTolerance = true
  FormatSpec = %.2f
  FormatSpecOverTolerance = %+.2f
  FormatSpecUnderTolerance = %+.2f
  Inverted = false
  LockPosition = false
  MeasureType = 1
  OverTolerance = 0
  References2D = -> [ProjItem008]
  Rotation = 0
  ScaleType = 0
  TheoreticalExact = false
  Type = 2
  UnderTolerance = 0
  X = -105.388
  Y = 36.9146
FEATURE [TechDraw::DrawViewDimension] Dimension026
  Arbitrary = false
  ArbitraryTolerances = false
  EqualTolerance = true
  FormatSpec = %.2f
  FormatSpecOverTolerance = %+.2f
  FormatSpecUnderTolerance = %+.2f
  Inverted = false
  LockPosition = false
  MeasureType = 1
  OverTolerance = 0
  References2D = -> [ProjItem008]
  Rotation = 0
  ScaleType = 0
  TheoreticalExact = false
  Type = 0
  UnderTolerance = 0
  X = -51.5113
  Y = 39.2129
FEATURE [TechDraw::DrawViewDimension] Dimension027
  Arbitrary = false
  ArbitraryTolerances = false
  EqualTolerance = true
  FormatSpec = %.2f
  FormatSpecOverTolerance = %+.2f
  FormatSpecUnderTolerance = %+.2f
  Inverted = false
  LockPosition = false
  MeasureType = 1
  OverTolerance = 0
  References2D = -> [ProjItem008]
  Rotation = 0
  ScaleType = 0
  TheoreticalExact = false
  Type = 1
  UnderTolerance = 0
  X = 0.508589
  Y = 55.469
FEATURE [TechDraw::DrawViewDimension] Dimension029
  Arbitrary = false
  ArbitraryTolerances = false
  EqualTolerance = true
  FormatSpec = %.2f
  FormatSpecOverTolerance = %+.2f
  FormatSpecUnderTolerance = %+.2f
  Inverted = false
  LockPosition = false
  MeasureType = 1
  OverTolerance = 0
  References2D = -> [ProjItem008]
  Rotation = 0
  ScaleType = 0
  TheoreticalExact = false
  Type = 1
  UnderTolerance = 0
  X = -45.9654
  Y = -41.2316
FEATURE [TechDraw::DrawViewDimension] Dimension030
  Arbitrary = false
  ArbitraryTolerances = false
  EqualTolerance = true
  FormatSpec = %.2f
  FormatSpecOverTolerance = %+.2f
  FormatSpecUnderTolerance = %+.2f
  Inverted = false
  LockPosition = false
  MeasureType = 1
  OverTolerance = 0
  References2D = -> [ProjItem008]
  Rotation = 0
  ScaleType = 0
  TheoreticalExact = false
  Type = 1
  UnderTolerance = 0
  X = 0.043413
  Y = -53.1483
FEATURE [TechDraw::DrawViewDimension] Dimension031
  Arbitrary = false
  ArbitraryTolerances = false
  EqualTolerance = true
  FormatSpec = %.2f
  FormatSpecOverTolerance = %+.2f
  FormatSpecUnderTolerance = %+.2f
  Inverted = false
  LockPosition = false
  MeasureType = 1
  OverTolerance = 0
  References2D = -> [ProjItem008]
  Rotation = 0
  ScaleType = 0
  TheoreticalExact = false
  Type = 2
  UnderTolerance = 0
  X = 112.237
  Y = 0.421087
FEATURE [TechDraw::DrawViewDimension] Dimension032
  Arbitrary = false
  ArbitraryTolerances = false
  EqualTolerance = true
  FormatSpec = %.2f
  FormatSpecOverTolerance = %+.2f
  FormatSpecUnderTolerance = %+.2f
  Inverted = false
  LockPosition = false
  MeasureType = 1
  OverTolerance = 0
  References2D = -> [ProjItem008]
  Rotation = 0
  ScaleType = 0
  TheoreticalExact = false
  Type = 2
  UnderTolerance = 0
  X = 18.123
  Y = 10.5794
FEATURE [TechDraw::DrawViewDimension] Dimension033
  Arbitrary = false
  ArbitraryTolerances = false
  EqualTolerance = true
  FormatSpec = %.2f
  FormatSpecOverTolerance = %+.2f
  FormatSpecUnderTolerance = %+.2f
  Inverted = false
  LockPosition = false
  MeasureType = 1
  OverTolerance = 0
  References2D = -> [ProjItem008]
  Rotation = 0
  ScaleType = 0
  TheoreticalExact = false
  Type = 1
  UnderTolerance = 0
  X = -46.7421
  Y = -6.74777
FEATURE [TechDraw::DrawViewDimension] Dimension034
  Arbitrary = false
  ArbitraryTolerances = false
  EqualTolerance = true
  FormatSpec = ⌀%.2f
  FormatSpecOverTolerance = %+.2f
  FormatSpecUnderTolerance = %+.2f
  Inverted = false
  LockPosition = false
  MeasureType = 1
  OverTolerance = 0
  References2D = -> [ProjItem008]
  Rotation = 0
  ScaleType = 0
  TheoreticalExact = false
  Type = 5
  UnderTolerance = 0
  X = -52.5109
  Y = 10.3438
FEATURE [TechDraw::DrawViewDimension] Dimension035
  Arbitrary = false
  ArbitraryTolerances = false
  EqualTolerance = true
  FormatSpec = ⌀%.2f
  FormatSpecOverTolerance = %+.2f
  FormatSpecUnderTolerance = %+.2f
  Inverted = false
  LockPosition = false
  MeasureType = 1
  OverTolerance = 0
  References2D = -> [ProjItem008]
  Rotation = 0
  ScaleType = 0
  TheoreticalExact = false
  Type = 5
  UnderTolerance = 0
  X = 43.2301
  Y = 16.7834
FEATURE [TechDraw::DrawViewDimension] Dimension038
  Arbitrary = false
  ArbitraryTolerances = false
  EqualTolerance = true
  FormatSpec = %.2f
  FormatSpecOverTolerance = %+.2f
  FormatSpecUnderTolerance = %+.2f
  Inverted = false
  LockPosition = false
  MeasureType = 1
  OverTolerance = 0
  References2D = -> [ProjItem009]
  Rotation = 0
  ScaleType = 0
  TheoreticalExact = false
  Type = 2
  UnderTolerance = 0
  X = -82.3237
  Y = 0
FEATURE [TechDraw::DrawViewDimension] Dimension040
  Arbitrary = false
  ArbitraryTolerances = false
  EqualTolerance = true
  FormatSpec = %.2f
  FormatSpecOverTolerance = %+.2f
  FormatSpecUnderTolerance = %+.2f
  Inverted = false
  LockPosition = false
  MeasureType = 1
  OverTolerance = 0
  References2D = -> [ProjItem005]
  Rotation = 0
  ScaleType = 0
  TheoreticalExact = false
  Type = 1
  UnderTolerance = 0
  X = -89.0705
  Y = 59.4471
FEATURE [TechDraw::DrawViewDimension] Dimension041
  Arbitrary = false
  ArbitraryTolerances = false
  EqualTolerance = true
  FormatSpec = %.2f
  FormatSpecOverTolerance = %+.2f
  FormatSpecUnderTolerance = %+.2f
  Inverted = false
  LockPosition = false
  MeasureType = 1
  OverTolerance = 0
  References2D = -> [ProjItem005]
  Rotation = 0
  ScaleType = 0
  TheoreticalExact = false
  Type = 2
  UnderTolerance = 0
  X = 98.0822
  Y = 0
FEATURE [TechDraw::DrawViewDimension] Dimension042
  Arbitrary = false
  ArbitraryTolerances = false
  EqualTolerance = true
  FormatSpec = %.2f
  FormatSpecOverTolerance = %+.2f
  FormatSpecUnderTolerance = %+.2f
  Inverted = false
  LockPosition = false
  MeasureType = 1
  OverTolerance = 0
  References2D = -> [ProjItem008]
  Rotation = 0
  ScaleType = 0
  TheoreticalExact = false
  Type = 1
  UnderTolerance = 0
  X = -88.764
  Y = 10.8621
FEATURE [TechDraw::DrawViewDimension] Dimension043
  Arbitrary = false
  ArbitraryTolerances = false
  EqualTolerance = true
  FormatSpec = %.2f
  FormatSpecOverTolerance = %+.2f
  FormatSpecUnderTolerance = %+.2f
  Inverted = false
  LockPosition = false
  MeasureType = 1
  OverTolerance = 0
  References2D = -> [ProjItem008]
  Rotation = 0
  ScaleType = 0
  TheoreticalExact = false
  Type = 2
  UnderTolerance = 0
  X = 101.592
  Y = 10.3341
FEATURE [TechDraw::DrawViewDimension] Dimension044
  Arbitrary = false
  ArbitraryTolerances = false
  EqualTolerance = true
  FormatSpec = %.2f
  FormatSpecOverTolerance = %+.2f
  FormatSpecUnderTolerance = %+.2f
  Inverted = false
  LockPosition = false
  MeasureType = 1
  OverTolerance = 0
  References2D = -> [ProjItem008]
  Rotation = 0
  ScaleType = 0
  TheoreticalExact = false
  Type = 2
  UnderTolerance = 0
  X = 101.856
  Y = -5.05375
FEATURE [TechDraw::DrawViewDimension] Dimension045
  Arbitrary = false
  ArbitraryTolerances = false
  EqualTolerance = true
  FormatSpec = %.2f
  FormatSpecOverTolerance = %+.2f
  FormatSpecUnderTolerance = %+.2f
  Inverted = false
  LockPosition = false
  MeasureType = 1
  OverTolerance = 0
  References2D = -> [ProjItem008]
  Rotation = 0
  ScaleType = 0
  TheoreticalExact = false
  Type = 1
  UnderTolerance = 0
  X = -73.5
  Y = -4.75229
FEATURE [TechDraw::DrawViewDimension] Dimension046
  Arbitrary = false
  ArbitraryTolerances = false
  EqualTolerance = true
  FormatSpec = %.2f
  FormatSpecOverTolerance = %+.2f
  FormatSpecUnderTolerance = %+.2f
  Inverted = false
  LockPosition = false
  MeasureType = 1
  OverTolerance = 0
  References2D = -> [ProjItem008]
  Rotation = 0
  ScaleType = 0
  TheoreticalExact = false
  Type = 1
  UnderTolerance = 0
  X = 45.3879
  Y = -44.6189
FEATURE [TechDraw::DrawPage] Page002  label="Крепление лепестков001"
  KeepUpdated = true
  NextBalloonIndex = 1
  ProjectionType = 0
  Template = -> Template002
  Views = -> [ProjGroup003,Dimension024,Dimension025,Dimension026,Dimension027,Dimension029,Dimension030,Dimension031,Dimension032,Dimension033,Dimension034,Dimension035,Dimension038,ProjGroup004,Dimension042,Dimension043,Dimension044,Dimension045,Dimension046]
FEATURE [TechDraw::DrawViewDimension] Dimension047
  Arbitrary = false
  ArbitraryTolerances = false
  EqualTolerance = true
  FormatSpec = %.2f
  FormatSpecOverTolerance = %+.2f
  FormatSpecUnderTolerance = %+.2f
  Inverted = false
  LockPosition = false
  MeasureType = 1
  OverTolerance = 0
  References2D = -> [ProjItem005]
  Rotation = 0
  ScaleType = 0
  TheoreticalExact = false
  Type = 0
  UnderTolerance = 0
  X = -107.09
  Y = 35.694
FEATURE [TechDraw::DrawViewDimension] Dimension048
  Arbitrary = false
  ArbitraryTolerances = false
  EqualTolerance = true
  FormatSpec = %.2f
  FormatSpecOverTolerance = %+.2f
  FormatSpecUnderTolerance = %+.2f
  Inverted = false
  LockPosition = false
  MeasureType = 1
  OverTolerance = 0
  References2D = -> [ProjItem005]
  Rotation = 0
  ScaleType = 0
  TheoreticalExact = false
  Type = 2
  UnderTolerance = 0
  X = -45.8889
  Y = 23.4816
FEATURE [TechDraw::DrawViewDimension] Dimension049
  Arbitrary = false
  ArbitraryTolerances = false
  EqualTolerance = true
  FormatSpec = %.2f
  FormatSpecOverTolerance = %+.2f
  FormatSpecUnderTolerance = %+.2f
  Inverted = false
  LockPosition = false
  MeasureType = 1
  OverTolerance = 0
  References2D = -> [ProjItem005]
  Rotation = 0
  ScaleType = 0
  TheoreticalExact = false
  Type = 0
  UnderTolerance = 0
  X = -66.7385
  Y = 18.3735
FEATURE [TechDraw::DrawPage] Page001  label="Крепление кнопок"
  KeepUpdated = true
  NextBalloonIndex = 1
  ProjectionType = 0
  Template = -> Template001
  Views = -> [ProjGroup002,Dimension008,Dimension011,Dimension012,Dimension013,Dimension014,Dimension016,Dimension022,Dimension023,Dimension040,Dimension041,Dimension047,Dimension048,Dimension049]
FEATURE [App::DocumentObjectGroup] Group  label="Чертежи"
  Group = -> [Page,Page001,Page002]
FEATURE [App::Link] Link001  label="PaddleShifter v2"
  LinkPlacement = pos=(65,0.099993,-14) rot=(1,0,0;3.14159rad)
  LinkedObject = -> <external PaddleShifter-v2.FCStd>#Part
  Placement = pos=(65,0.099993,-14) rot=(1,0,0;3.14159rad)
FEATURE [App::Part] Part004  label="Крепление лепестков002"
  Group = -> [Body003,Link,Link001]
  Origin = -> Origin008
FEATURE [App::Part] Part001  label="Крепление руля"
  Group = -> [Body,Body001,Body002,Part002,Part004]
  LabelDocUser = Wheel
  LabelPartUser = Крепление руля
  Origin = -> Origin002
  PadLengthUser = 6.0 
  ShapeLengthUser = 462.24
  ShapeVolumeUser = 6.0 mm x 100.0 mm x 150.0 mm
FEATURE [App::Part] Part  label="Wheel"
  Group = -> [steering_wheel_momo_team,Part001,Feature,Part003]
  Origin = -> Origin
FEATURE [Part::Mirroring] mirror  label="PaddleShifter v2 (mirrored)"
  Base = (0,-42.5,-14)
  Normal = (1,0,0)
  Source = -> Link001

RESOLVED EXTERNAL PARTS (link-assembly join: the EXTERNAL_REF files above that resolve inside this repo's crawl, each included once):
---- part PaddleShifter-v2.FCStd = doc fcstd_8c9d927928c2 (50414 chars; too large to inline — full recipe in that document) ----
---- part PaddleShifter.FCStd = doc fcstd_9a16fa72eb6d ----
FCSTD DOCUMENT  (FreeCAD 0.19R24267 +99 (Git))
Label: PaddleShifter
License: All rights reserved
LicenseURL: http://en.wikipedia.org/wiki/All_rights_reserved
objects: Part::FeaturePython×14, Sketcher::SketchObject×14, PartDesign::Pocket×9, PartDesign::Pad×7, PartDesign::Body×7, App::Part×3, PartDesign::ShapeBinder×2, PartDesign::SubShapeBinder×2, Part::Feature×1
note: 72 computed .brp shape members not serialized (recipe doc carries the construction recipe); baked Part::Feature solids carry a one-line shape summary decoded from their .brp

FEATURE [Part::FeaturePython] Screw006  label="M2x10-Screw001"  # Fasteners workbench fastener (typed FeaturePython)
  Placement = pos=(30,3.25,11) rot=(0,1,0;1.5708rad)
  baseObject = -> Body [Edge35]
  diameter = 2
  invert = false
  length = 5
  lengthCustom = 10
  matchOuter = true
  offset = 6
  thread = false
  type = 34
FEATURE [Part::FeaturePython] Screw005  label="M2x10-Screw"  # Fasteners workbench fastener (typed FeaturePython)
  Placement = pos=(30,-3.25,11) rot=(0,1,0;1.5708rad)
  baseObject = -> Body [Edge34]
  diameter = 2
  invert = false
  length = 5
  lengthCustom = 10
  matchOuter = true
  offset = 6
  thread = false
  type = 34
FEATURE [Part::FeaturePython] Nut004  label="M6-Nut086"  # Fasteners workbench fastener (typed FeaturePython)
  Placement = pos=(-7,26.3866,8) rot=(1,0,0;1.5708rad)
  baseObject = -> Screw003 [Edge39]
  diameter = 8
  invert = false
  matchOuter = true
  offset = 2
  thread = false
  type = 7
FEATURE [Part::FeaturePython] Nut003  label="M6-Nut085"  # Fasteners workbench fastener (typed FeaturePython)
  Placement = pos=(7,26.3866,8) rot=(1,0,0;1.5708rad)
  baseObject = -> Screw004 [Edge39]
  diameter = 8
  invert = false
  matchOuter = true
  offset = 2
  thread = false
  type = 7
FEATURE [Part::FeaturePython] Nut002  label="M6-Nut"  # Fasteners workbench fastener (typed FeaturePython)
  Placement = pos=(-1e-15,26.3866,36) rot=(1,0,0;1.5708rad)
  baseObject = -> Screw002 [Edge39]
  diameter = 8
  invert = false
  matchOuter = true
  offset = 2
  thread = false
  type = 7
FEATURE [Part::FeaturePython] Screw004  label="M6x50-Screw078"  # Fasteners workbench fastener (typed FeaturePython)
  Placement = pos=(7,-21,8) rot=(1,0,0;1.5708rad)
  baseObject = -> Body001 [Edge16]
  diameter = 8
  invert = false
  length = 9
  lengthCustom = 50
  matchOuter = true
  offset = 0
  thread = false
  type = 29
FEATURE [Part::FeaturePython] Screw003  label="M6x50-Screw077"  # Fasteners workbench fastener (typed FeaturePython)
  Placement = pos=(-7,-21,8) rot=(1,0,0;1.5708rad)
  baseObject = -> Body001 [Edge17]
  diameter = 8
  invert = false
  length = 9
  lengthCustom = 50
  matchOuter = true
  offset = 0
  thread = false
  type = 29
FEATURE [Part::FeaturePython] Screw002  label="M6x50-Screw"  # Fasteners workbench fastener (typed FeaturePython)
  Placement = pos=(-1e-15,-21,36) rot=(1,0,0;1.5708rad)
  baseObject = -> Body001 [Edge18]
  diameter = 8
  invert = true
  length = 9
  lengthCustom = 50
  matchOuter = true
  offset = 0
  thread = false
  type = 29
FEATURE [Part::Feature] Part__Feature  label="Switch"
  Placement = pos=(27,1.5e-14,9.5) rot=(0,0,1;1.5708rad)
  shape: bbox 7.341 x 13.39 x 13 mm, 256 faces, 7 solids (baked)
FEATURE [PartDesign::ShapeBinder] ShapeBinder001
  Placement = pos=(27,1.5e-14,9.5) rot=(0,0,1;1.5708rad)
  Support = -> [Part__Feature]
  TraceSupport = false
FEATURE [Sketcher::SketchObject] Sketch
  FullyConstrained = true
  MapMode = 5
  Support = -> [XY_Plane001]
  sketch-geometry (10):
    g0: LineSegment StartX=-22 StartY=15 StartZ=0 EndX=30 EndY=15 EndZ=0
    g1: LineSegment StartX=30 StartY=-15 StartZ=0 EndX=-22 EndY=-15 EndZ=0
    g2: LineSegment StartX=-22 StartY=-15 StartZ=0 EndX=-22 EndY=15 EndZ=0
    g3: GeomPoint X=0 Y=15 Z=0
    g4: GeomPoint X=-22 Y=0 Z=0
    g5: LineSegment StartX=30 StartY=15 StartZ=0 EndX=30 EndY=6.5 EndZ=0
    g6: LineSegment StartX=30 StartY=-15 StartZ=0 EndX=30 EndY=-6.5 EndZ=0
    g7: LineSegment StartX=30 StartY=-6.5 StartZ=0 EndX=24 EndY=-6.5 EndZ=0
    g8: LineSegment StartX=24 StartY=-6.5 StartZ=0 EndX=24 EndY=6.5 EndZ=0
    g9: LineSegment StartX=24 StartY=6.5 StartZ=0 EndX=30 EndY=6.5 EndZ=0
  constraints (27):
    c: Coincident(g1,g2)
    c: Coincident(g2,g0)
    c: Horizontal(g0)
    c: Horizontal(g1)
    c: Vertical(g2)
    c: DistanceY(g1,g0) = 30
    c: PointOnObject(g3,g-2)
    c: PointOnObject(g3,g0)
    c: Distance(g3,g0) = 22
    c: Distance(g3,g0) = 30
    c: PointOnObject(g4,g-1)
    c: Symmetric(g0,g1,g4)
    c: Coincident(g5,g0)
    c: Vertical(g5)
    c: Coincident(g6,g1)
    c: Vertical(g6)
    c: Coincident(g7,g6)
    c: Horizontal(g7)
    c: Coincident(g8,g7)
    c: Vertical(g8)
    c: Coincident(g9,g8)
    c: Coincident(g9,g5)
    c: Horizontal(g9)
    c: DistanceY(g8,g8) = 13
    c: Equal(g7,g9)
    c: Equal(g5,g6)
    c: DistanceX(g7,g7) = 6
FEATURE [PartDesign::Pad] Pad
  Direction = (1,1,1)
  Length = 16
  Length2 = 100
  Profile = -> Sketch
  Type = 0
FEATURE [Sketcher::SketchObject] Sketch001
  FullyConstrained = true
  MapMode = 5
  Support = -> [XY_Plane002]
  sketch-geometry (4):
    g0: LineSegment StartX=-15 StartY=22.5 StartZ=0 EndX=15 EndY=22.5 EndZ=0
    g1: LineSegment StartX=15 StartY=22.5 StartZ=0 EndX=15 EndY=-22.5 EndZ=0
    g2: LineSegment StartX=15 StartY=-22.5 StartZ=0 EndX=-15 EndY=-22.5 EndZ=0
    g3: LineSegment StartX=-15 StartY=-22.5 StartZ=0 EndX=-15 EndY=22.5 EndZ=0
  constraints (11):
    c: Coincident(g0,g1)
    c: Coincident(g1,g2)
    c: Coincident(g2,g3)
    c: Coincident(g3,g0)
    c: Horizontal(g0)
    c: Horizontal(g2)
    c: Vertical(g1)
    c: Vertical(g3)
    c: Symmetric(g2,g0,g-1)
    c: DistanceX(g0,g0) = 30
    c: DistanceY(g1,g1) = 45
FEATURE [PartDesign::Pad] Pad001
  Direction = (1,1,1)
  Length = 6
  Length2 = 100
  Profile = -> Sketch001
  Type = 0
FEATURE [Sketcher::SketchObject] Sketch003
  ExternalGeometry = -> [Pad001]
  FullyConstrained = false
  MapMode = 5
  Placement = pos=(0,0,6) rot=(0,0,1;0rad)
  Support = -> [Pad001]
  sketch-geometry (5):
    g0: Circle CenterX=7 CenterY=-14.5 CenterZ=0 NormalX=0 NormalY=0 NormalZ=1 AngleXU=0 Radius=3
    g1: Circle CenterX=-7 CenterY=-14.5 CenterZ=0 NormalX=0 NormalY=0 NormalZ=1 AngleXU=0 Radius=3
    g2: LineSegment StartX=-15 StartY=-14.5 StartZ=0 EndX=15 EndY=-14.5 EndZ=0
    g3: GeomPoint X=0 Y=-14.5 Z=0
    g4: Circle CenterX=7e-16 CenterY=16 CenterZ=0 NormalX=0 NormalY=0 NormalZ=1 AngleXU=0 Radius=3
  constraints (11):
    c: PointOnObject(g2,g-3)
    c: PointOnObject(g2,g-5)
    c: Horizontal(g2)
    c: PointOnObject(g1,g2)
    c: PointOnObject(g0,g2)
    c: Distance(g2,g-4) = 8
    c: Distance(g1,g2) = 8
    c: PointOnObject(g3,g-2)
    c: Symmetric(g0,g1,g3)
    c: Diameter(g0) = 6
    c: Equal(g0,g1)
FEATURE [PartDesign::Pocket] Pocket
  BaseFeature = -> Pad001
  Length = 5
  Length2 = 100
  Profile = -> Sketch003
  Type = 1
FEATURE [PartDesign::SubShapeBinder] Binder
  BindMode = 0
  ClaimChildren = false
  Context = -> Part [Body001.Binder.]
  Fuse = false
  MakeFace = true
  PartialLoad = false
  Relative = true
  Support = -> [Part001[Body004.Pocket002.Edge15]]
  _Version = 2
FEATURE [PartDesign::Pocket] Pocket008
  BaseFeature = -> Pocket
  Length = 5
  Length2 = 100
  Profile = -> Binder
  Reversed = true
  Type = 1
FEATURE [PartDesign::Body] Body001  label="Крепление"
  Group = -> [Sketch001,Pad001,Sketch003,Pocket,Binder,Pocket008]
  Origin = -> Origin002
  Placement = pos=(-3e-15,-15,22.5) rot=(1,0,0;1.5708rad)
  Tip = -> Pocket008
FEATURE [PartDesign::ShapeBinder] ShapeBinder
  Placement = pos=(-3e-15,-15,22.5) rot=(1,0,0;1.5708rad)
  Support = -> [Body001]
  TraceSupport = false
FEATURE [Sketcher::SketchObject] Sketch004
  ExternalGeometry = -> [ShapeBinder]
  FullyConstrained = false
  MapMode = 5
  Placement = pos=(0,15,0) rot=(0,0.707107,0.707107;3.14159rad)
  Support = -> [Pad]
  sketch-geometry (3):
    g0: Circle CenterX=7 CenterY=8 CenterZ=0 NormalX=0 NormalY=0 NormalZ=1 AngleXU=0 Radius=3
    g1: Circle CenterX=-9e-16 CenterY=31 CenterZ=0 NormalX=0 NormalY=0 NormalZ=1 AngleXU=0 Radius=3
    g2: Circle CenterX=-7 CenterY=8 CenterZ=0 NormalX=0 NormalY=0 NormalZ=1 AngleXU=0 Radius=3
FEATURE [PartDesign::Pocket] Pocket001
  BaseFeature = -> Pad
  Length = 5
  Length2 = 100
  Profile = -> Sketch004
  Type = 1
FEATURE [Sketcher::SketchObject] Sketch009
  ExternalGeometry = -> [Pocket001]
  FullyConstrained = true
  MapMode = 5
  Placement = pos=(0,0,16) rot=(0,0,1;0rad)
  Support = -> [Pocket001]
  sketch-geometry (2):
    g0: Circle CenterX=0 CenterY=0 CenterZ=0 NormalX=0 NormalY=0 NormalZ=1 AngleXU=0 Radius=3
    g1: Circle CenterX=17 CenterY=0 CenterZ=0 NormalX=0 NormalY=0 NormalZ=1 AngleXU=0 Radius=3
  constraints (5):
    c: Diameter(g0) = 6
    c: PointOnObject(g1,g-1)
    c: Equal(g0,g1)
    c: Distance(g1,g-6) = 13
    c: Coincident(g0,g-1)
FEATURE [PartDesign::Pocket] Pocket003
  BaseFeature = -> Pocket001
  Length = 5
  Length2 = 100
  Profile = -> Sketch009
  Type = 1
FEATURE [Sketcher::SketchObject] Sketch011
  ExternalGeometry = -> [Pocket003]
  FullyConstrained = true
  MapMode = 5
  Placement = pos=(24,0,0) rot=(0.57735,0.57735,0.57735;2.0944rad)
  Support = -> [Pocket003]
  sketch-geometry (3):
    g0: Circle CenterX=3.25 CenterY=11 CenterZ=0 NormalX=0 NormalY=0 NormalZ=1 AngleXU=0 Radius=1
    g1: Circle CenterX=-3.25 CenterY=11 CenterZ=0 NormalX=0 NormalY=0 NormalZ=1 AngleXU=0 Radius=1
    g2: LineSegment StartX=-3.25 StartY=11 StartZ=0 EndX=3.25 EndY=11 EndZ=0
  constraints (8):
    c: Diameter(g0) = 2
    c: DistanceX(g-2,g0) = 3.25
    c: Equal(g1,g0)
    c: Coincident(g2,g1)
    c: Coincident(g2,g0)
    c: Horizontal(g2)
    c: DistanceX(g-2,g1) = -3.25
    c: Distance(g1,g-3) = 5
FEATURE [PartDesign::Pocket] Pocket005
  BaseFeature = -> Pocket003
  Length = 5
  Length2 = 100
  Profile = -> Sketch011
  Type = 0
FEATURE [PartDesign::Body] Body  label="Основа"
  Group = -> [Sketch,Pad,ShapeBinder,Sketch004,Pocket001,Sketch009,Pocket003,ShapeBinder001,Sketch011,Pocket005]
  Origin = -> Origin001
  Tip = -> Pocket005
FEATURE [Part::FeaturePython] Nut  label="M4-Nut"  # Fasteners workbench fastener (typed FeaturePython)
  Placement = pos=(42,-7,12) rot=(0,0,1;0rad)
  baseObject = -> Screw001 [Edge7]
  diameter = 6
  invert = false
  matchOuter = false
  offset = 0
  thread = false
  type = 7
FEATURE [Part::FeaturePython] Screw001  label="M4x16-Screw"  # Fasteners workbench fastener (typed FeaturePython)
  Placement = pos=(42,-7,28) rot=(0,0,1;0rad)
  baseObject = -> Body002 [Edge16]
  diameter = 6
  invert = false
  length = 6
  lengthCustom = 16
  matchOuter = false
  offset = 0
  thread = false
  type = 35
FEATURE [Sketcher::SketchObject] Sketch012
  FullyConstrained = false
  MapMode = 5
  Support = -> [XY_Plane009]
  sketch-geometry (13):
    g0: LineSegment StartX=-10 StartY=55 StartZ=0 EndX=10 EndY=55 EndZ=0
    g1: LineSegment StartX=10 StartY=55 StartZ=0 EndX=10 EndY=-55 EndZ=0
    g2: LineSegment StartX=10 StartY=-55 StartZ=0 EndX=-10 EndY=-55 EndZ=0
    g3: LineSegment StartX=-10 StartY=-55 StartZ=0 EndX=-10 EndY=55 EndZ=0
    g4: LineSegment StartX=10 StartY=55 StartZ=0 EndX=-10 EndY=55 EndZ=0
    g5: LineSegment StartX=0 StartY=14.1646 StartZ=0 EndX=-12 EndY=14.1646 EndZ=0
    g6: LineSegment StartX=7e-16 StartY=-15.8354 StartZ=0 EndX=-12 EndY=-15.8354 EndZ=0
    g7: LineSegment StartX=-12 StartY=14.1646 StartZ=0 EndX=-12 EndY=-15.8354 EndZ=0
    g8: LineSegment StartX=10 StartY=-55 StartZ=0 EndX=-10 EndY=-55 EndZ=0
    g9: ArcOfCircle CenterX=-83.3333 CenterY=1e-15 CenterZ=0 NormalX=0 NormalY=0 NormalZ=1 AngleXU=0 Radius=108.333 StartAngle=5.75068 EndAngle=6.81569
    g10: ArcOfCircle CenterX=-98.5179 CenterY=-11.5395 CenterZ=0 NormalX=0 NormalY=0 NormalZ=1 AngleXU=0 Radius=98.6115 StartAngle=5.82678 EndAngle=6.23961
    g11: ArcOfCircle CenterX=-98.5798 CenterY=11.666 CenterZ=0 NormalX=0 NormalY=0 NormalZ=1 AngleXU=0 Radius=98.6115 StartAngle=0.025341 EndAngle=0.454978
    g12: GeomPoint X=25 Y=0 Z=0
  constraints (34):
    c: Coincident(g0,g1)
    c: Coincident(g2,g3)
    c: Coincident(g3,g0)
    c: Horizontal(g0)
    c: Horizontal(g2)
    c: Coincident(g7,g5)
    c: Coincident(g7,g6)
    c: Equal(g5,g6)
    c: Vertical(g7)
    c: Coincident(g8,g2)
    c: Horizontal(g5)
    c: Horizontal(g6)
    c: Coincident(g4,g0)
    c: DistanceX(g0,g0) = 20
    c: PointOnObject(g5,g-2)
    c: DistanceY(g7,g7) = 30
    c: Coincident(g9,g4)
    c: Vertical(g3)
    c: Vertical(g1)
    c: Coincident(g10,g6)
    c: Coincident(g10,g8)
    c: Coincident(g11,g4)
    c: Coincident(g11,g5)
    c: Equal(g11,g10)
    c: DistanceY(g8,g4) = 110
    c: PointOnObject(g12,g9)
    c: PointOnObject(g12,g-1)
    c: Distance(g-1,g12) = 25
    c: DistanceX(g5,g5) = 12
    c: Coincident(g8,g1)
    c: Coincident(g8,g9)
    c: Coincident(g8,g2)
    c: Coincident(g4,g0)
    c: Symmetric(g8,g4,g-1)
FEATURE [PartDesign::Pad] Pad006
  Direction = (1,1,1)
  Length = 6
  Length2 = 100
  Profile = -> Sketch012
  Type = 0
FEATURE [Sketcher::SketchObject] Sketch014
  ExternalGeometry = -> [Pad006]
  FullyConstrained = true
  MapMode = 5
  Placement = pos=(0,0,6) rot=(0,0,1;0rad)
  Support = -> [Pad006]
  sketch-geometry (3):
    g0: Circle CenterX=-6 CenterY=6.1646 CenterZ=0 NormalX=0 NormalY=0 NormalZ=1 AngleXU=0 Radius=2
    g1: Circle CenterX=-6 CenterY=-7.8354 CenterZ=0 NormalX=0 NormalY=0 NormalZ=1 AngleXU=0 Radius=2
    g2: LineSegment StartX=-6 StartY=14.1646 StartZ=0 EndX=-6 EndY=-15.8354 EndZ=0
  constraints (10):
    c: Equal(g0,g1)
    c: Diameter(g0) = 4
    c: PointOnObject(g2,g-3)
    c: PointOnObject(g2,g-5)
    c: Vertical(g2)
    c: PointOnObject(g0,g2)
    c: PointOnObject(g1,g2)
    c: Distance(g0,g2) = 8
    c: Distance(g1,g2) = 8
    c: Distance(g2,g-4) = 6
FEATURE [PartDesign::Pocket] Pocket007
  BaseFeature = -> Pad006
  Length = 5
  Length2 = 100
  Profile = -> Sketch014
  Type = 1
FEATURE [PartDesign::Body] Body006  label="Лепесток"
  Group = -> [Sketch012,Pad006,Sketch014,Pocket007]
  Origin = -> Origin009
  Placement = pos=(48,0.8354,16) rot=(0,0,1;0rad)
  Tip = -> Pocket007
FEATURE [Sketcher::SketchObject] Sketch007
  FullyConstrained = true
  MapMode = 5
  Support = -> [XY_Plane005]
  sketch-geometry (4):
    g0: LineSegment StartX=-10 StartY=15 StartZ=0 EndX=10 EndY=15 EndZ=0
    g1: LineSegment StartX=10 StartY=15 StartZ=0 EndX=10 EndY=-15 EndZ=0
    g2: LineSegment StartX=10 StartY=-15 StartZ=0 EndX=-10 EndY=-15 EndZ=0
    g3: LineSegment StartX=-10 StartY=-15 StartZ=0 EndX=-10 EndY=15 EndZ=0
  constraints (11):
    c: Coincident(g0,g1)
    c: Coincident(g1,g2)
    c: Coincident(g2,g3)
    c: Coincident(g3,g0)
    c: Horizontal(g0)
    c: Horizontal(g2)
    c: Vertical(g1)
    c: Vertical(g3)
    c: Symmetric(g0,g2,g-1)
    c: DistanceX(g0,g0) = 20
    c: DistanceY(g1,g1) = 30
FEATURE [PartDesign::Pad] Pad004
  Direction = (1,1,1)
  Length = 16
  Length2 = 100
  Profile = -> Sketch007
  Type = 0
FEATURE [Sketcher::SketchObject] Sketch008
  ExternalGeometry = -> [Pad004]
  FullyConstrained = true
  MapMode = 5
  Placement = pos=(0,15,0) rot=(0,0.707107,0.707107;3.14159rad)
  Support = -> [Pad004]
  sketch-geometry (1):
    g0: Circle CenterX=1.1e-15 CenterY=8 CenterZ=0 NormalX=0 NormalY=0 NormalZ=1 AngleXU=0 Radius=3
  constraints (2):
    c: Diameter(g0) = 6
    c: Symmetric(g-3,g-5,g0)
FEATURE [PartDesign::Pocket] Pocket002
  BaseFeature = -> Pad004
  Length = 5
  Length2 = 100
  Profile = -> Sketch008
  Type = 1
FEATURE [PartDesign::Body] Body004  label="Крепление рычага"
  Group = -> [Sketch007,Pad004,Sketch008,Pocket002]
  Origin = -> Origin005
  Placement = pos=(0,0,28) rot=(0,0,1;0rad)
  Tip = -> Pocket002
FEATURE [Sketcher::SketchObject] Sketch005
  FullyConstrained = true
  MapMode = 5
  Support = -> [XY_Plane003]
  sketch-geometry (4):
    g0: LineSegment StartX=-35 StartY=15 StartZ=0 EndX=35 EndY=15 EndZ=0
    g1: LineSegment StartX=35 StartY=15 StartZ=0 EndX=35 EndY=-15 EndZ=0
    g2: LineSegment StartX=35 StartY=-15 StartZ=0 EndX=-35 EndY=-15 EndZ=0
    g3: LineSegment StartX=-35 StartY=-15 StartZ=0 EndX=-35 EndY=15 EndZ=0
  constraints (11):
    c: Coincident(g0,g1)
    c: Coincident(g1,g2)
    c: Coincident(g2,g3)
    c: Coincident(g3,g0)
    c: Horizontal(g0)
    c: Horizontal(g2)
    c: Vertical(g1)
    c: Vertical(g3)
    c: Symmetric(g0,g2,g-1)
    c: DistanceY(g1,g1) = 30
    c: DistanceX(g0,g0) = 70
FEATURE [PartDesign::Pad] Pad002
  Direction = (1,1,1)
  Length = 6
  Length2 = 100
  Profile = -> Sketch005
  Type = 0
FEATURE [PartDesign::SubShapeBinder] Binder001
  BindMode = 0
  ClaimChildren = false
  Context = -> Part [Part001.Body002.Binder001.]
  Fuse = false
  MakeFace = true
  PartialLoad = false
  Relative = true
  Support = -> [Part002[Body003.Pad003.Edge15]]
  _Version = 2
FEATURE [PartDesign::Pocket] Pocket004
  BaseFeature = -> Pad002
  Length = 5
  Length2 = 100
  Profile = -> Binder001
  Reversed = true
  Type = 1
FEATURE [Sketcher::SketchObject] Sketch013
  ExternalGeometry = -> [Pocket004]
  FullyConstrained = true
  MapMode = 5
  Placement = pos=(0,0,6) rot=(0,0,1;0rad)
  Support = -> [Pocket004]
  sketch-geometry (3):
    g0: Circle CenterX=29 CenterY=7 CenterZ=0 NormalX=0 NormalY=0 NormalZ=1 AngleXU=0 Radius=2
    g1: Circle CenterX=29 CenterY=-7 CenterZ=0 NormalX=0 NormalY=0 NormalZ=1 AngleXU=0 Radius=2
    g2: LineSegment StartX=29 StartY=15 StartZ=0 EndX=29 EndY=-15 EndZ=0
  constraints (10):
    c: Diameter(g0) = 4
    c: Equal(g0,g1)
    c: PointOnObject(g2,g-3)
    c: PointOnObject(g2,g-4)
    c: Vertical(g2)
    c: PointOnObject(g0,g2)
    c: PointOnObject(g1,g2)
    c: Distance(g0,g2) = 8
    c: Distance(g1,g2) = 8
    c: Distance(g2,g-3) = 6
FEATURE [PartDesign::Pocket] Pocket006
  BaseFeature = -> Pocket004
  Length = 5
  Length2 = 100
  Profile = -> Sketch013
  Type = 1
FEATURE [PartDesign::Body] Body002  label="Рычаг"
  Group = -> [Sketch005,Pad002,Binder001,Pocket004,Sketch013,Pocket006]
  Origin = -> Origin003
  Placement = pos=(13,0,22) rot=(0,0,1;0rad)
  Tip = -> Pocket006
FEATURE [Sketcher::SketchObject] Sketch006
  FullyConstrained = true
  MapMode = 5
  Support = -> [XY_Plane004]
  sketch-geometry (5):
    g0: LineSegment StartX=-8 StartY=15 StartZ=0 EndX=8 EndY=15 EndZ=0
    g1: LineSegment StartX=8 StartY=15 StartZ=0 EndX=8 EndY=-15 EndZ=0
    g2: LineSegment StartX=8 StartY=-15 StartZ=0 EndX=-8 EndY=-15 EndZ=0
    g3: LineSegment StartX=-8 StartY=-15 StartZ=0 EndX=-8 EndY=15 EndZ=0
    g4: Circle CenterX=0 CenterY=0 CenterZ=0 NormalX=0 NormalY=0 NormalZ=1 AngleXU=0 Radius=4
  constraints (13):
    c: Coincident(g0,g1)
    c: Coincident(g1,g2)
    c: Coincident(g2,g3)
    c: Coincident(g3,g0)
    c: Horizontal(g0)
    c: Horizontal(g2)
    c: Vertical(g1)
    c: Vertical(g3)
    c: Symmetric(g0,g2,g-1)
    c: DistanceX(g0,g0) = 16
    c: DistanceY(g1,g1) = 30
    c: Coincident(g4,g-1)
    c: Diameter(g4) = 8
FEATURE [PartDesign::Pad] Pad003
  Direction = (1,1,1)
  Length = 6
  Length2 = 100
  Profile = -> Sketch006
  Type = 0
FEATURE [PartDesign::Body] Body003  label="Проставка"
  Group = -> [Sketch006,Pad003]
  Origin = -> Origin004
  Tip = -> Pad003
FEATURE [Sketcher::SketchObject] Sketch010
  FullyConstrained = true
  MapMode = 5
  Support = -> [XY_Plane007]
  sketch-geometry (1):
    g0: Circle CenterX=0 CenterY=0 CenterZ=0 NormalX=0 NormalY=0 NormalZ=1 AngleXU=0 Radius=4
  constraints (2):
    c: Coincident(g0,g-1)
    c: Diameter(g0) = 8
FEATURE [PartDesign::Pad] Pad005
  Direction = (1,1,1)
  Length = 5
  Length2 = 100
  Profile = -> Sketch010
  Type = 0
FEATURE [PartDesign::Body] Body005  label="Неодимовый магнит (8х5)"
  Group = -> [Sketch010,Pad005]
  Origin = -> Origin007
  Placement = pos=(-14,0,22) rot=(0,0,1;0rad)
  Tip = -> Pad005
FEATURE [Part::FeaturePython] Clone  label="Неодимовый магнит (8х5)001"  # Draft clone (typed FeaturePython)
  AttacherType = Attacher::AttachEngine3D
  Fuse = false
  Objects = -> [Body005]
  Placement = pos=(4e-15,0,1) rot=(0,0,1;0rad)
  Scale = (1,1,1)
FEATURE [App::Part] Part002  label="Проставка001"
  Group = -> [Clone,Body003]
  Origin = -> Origin008
  Placement = pos=(-14,0,16) rot=(0,0,1;0rad)
FEATURE [Part::FeaturePython] Screw  label="M4x16-Screw001"  # Fasteners workbench fastener (typed FeaturePython)
  Placement = pos=(42,7,28) rot=(0,0,1;0rad)
  baseObject = -> Body002 [Edge18]
  diameter = 6
  invert = false
  length = 6
  lengthCustom = 16
  matchOuter = false
  offset = 0
  thread = false
  type = 35
FEATURE [Part::FeaturePython] Nut005  label="M4-Nut001"  # Fasteners workbench fastener (typed FeaturePython)
  Placement = pos=(42,7,12) rot=(0,0,1;0rad)
  baseObject = -> Screw [Edge7]
  diameter = 6
  invert = false
  matchOuter = false
  offset = 0
  thread = false
  type = 7
FEATURE [App::Part] Part001  label="Рычаг001"
  Group = -> [Body002,Body004,Body005,Body006,Screw001,Nut,Screw,Nut005]
  Origin = -> Origin006
FEATURE [Part::FeaturePython] Clone001  label="Крепление001"  # Draft clone (typed FeaturePython)
  AttacherType = Attacher::AttachEngine3D
  Fuse = false
  Objects = -> [Body001]
  Placement = pos=(-3e-15,21,22.5) rot=(1,0,0;1.5708rad)
  Scale = (1,1,1)
FEATURE [App::Part] Part  label="PaddleShifter"
  Group = -> [Body,Body001,Part__Feature,Part001,Part002,Screw002,Screw003,Screw004,Nut002,Nut003,Nut004,Screw005,Screw006,Clone001]
  Origin = -> Origin
